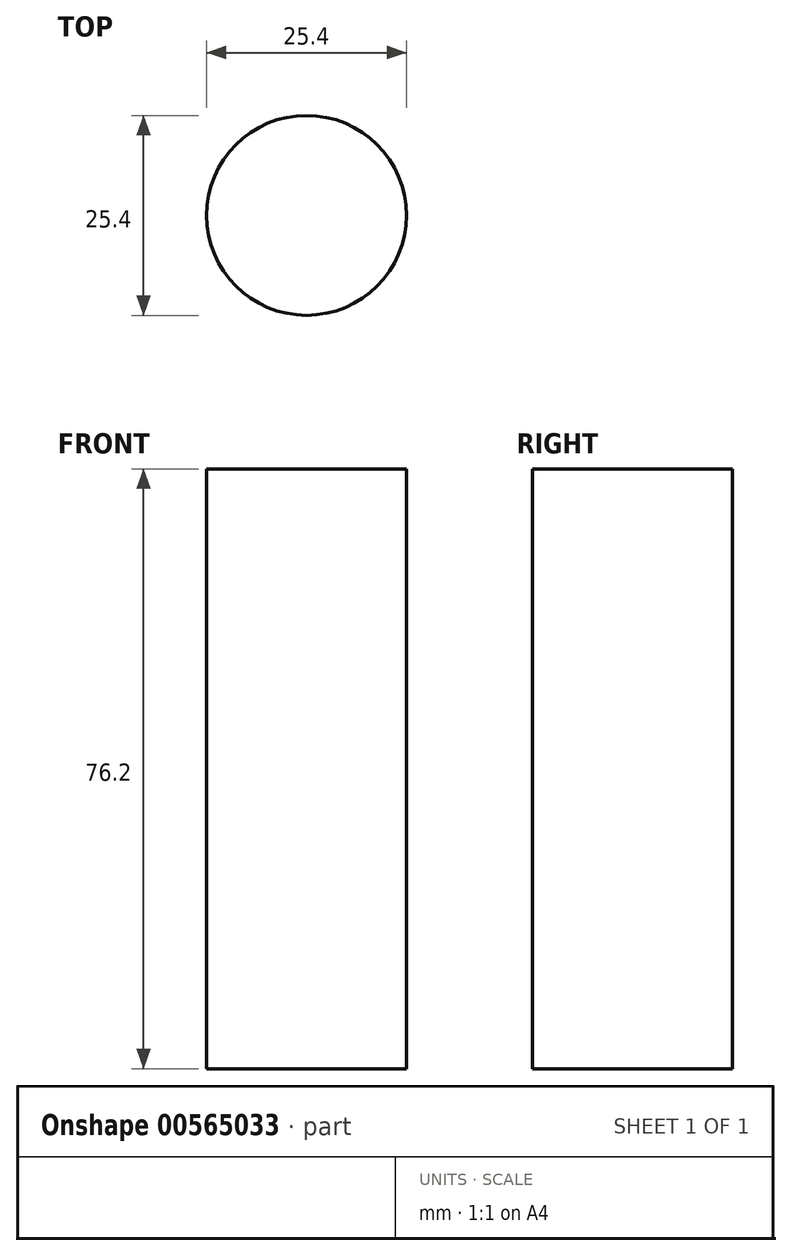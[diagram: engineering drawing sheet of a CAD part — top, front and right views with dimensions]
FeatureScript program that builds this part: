
annotation { "Feature Type Name" : "Feature", "Feature Type Description" : "" }
export const myFeature = defineFeature(function(context is Context, id is Id, definition is map)
    precondition{}
    {
        {
            var Q0;
            Q0=qCreatedBy(makeId("Front.planeOp"),FACE);
            var sketch = newSketch(context, id + "F0", { "sketchPlane" : qUnion([Q0])});
            skLineSegment(sketch, "E0", {"start": v(0, 0) * mm, "end": v(88.9, 0) * mm});
            skLineSegment(sketch, "E1", {"start": v(88.9, 0) * mm, "end": v(88.9, 1092.2) * mm});
            skLineSegment(sketch, "E2", {"start": v(88.9, 1092.2) * mm, "end": v(0, 1092.2) * mm});
            skLineSegment(sketch, "E3", {"start": v(0, 0) * mm, "end": v(0, 1191.58) * mm, "construction": true});
            skSolve(sketch);
        }
        {
            var Q0;
            Q0 = qSketchRegion(id + "F0", true);
            var Q1;
            Q1=sQuery(id+"F0.wireOp",EDGE,"E1");
            var Q2;
            Q2=sQuery(id+"F0.wireOp",EDGE,"E0");
            var Q3;
            Q3=sQuery(id+"F0.wireOp",EDGE,"E2");
            var Q4;
            Q4=sQuery(id+"F0.wireOp",EDGE,"Eqfm1BcG-SU4s-36cT-mnSU-gtJC7Ga610LP");
            var Q5;
            Q5=sQuery(id+"F0.wireOp",EDGE,"Ojjtict1-wwqD-w4ix-8k3J-fVzUUkNspiEs");
            var Q6;
            Q6=sQuery(id+"F0.wireOp",EDGE,"E3");
            revolve(context, id + "F1", {"bodyType" : ToolBodyType.SURFACE, "entities" : qUnion([Q0]), "surfaceEntities" : qUnion([Q1, Q2, Q3, Q4, Q5]), "axis" : qUnion([Q6]), "revolveType" : RevolveType.FULL});
        }
        {
            var Q0;
            Q0=makeQuery(id+"F1.opRevolve","SWEPT_EDGE",EDGE,{"disambiguationData":[OSD([sQuery(id+"F0.wireOp",VERTEX,"E2.start")])]});
            fillet(context, id + "F2", {"entities" : qUnion([Q0]), "radius" : 76.2 * mm, "tangentPropagation" : true, "allowEdgeOverflow" : false});
        }
        {
            var Q0;
            Q0=makeQuery(id+"F1.opRevolve","SWEPT_FACE",FACE,{"disambiguationData":[OSD([sQuery(id+"F0.wireOp",EDGE,"E2")])]});
            extrude(context, id + "F3", {"entities" : qUnion([Q0]), "oppositeDirection" : true, "depth" : 76.2 * mm, "offsetDistance" : 25.4 * mm});
        }
    });
